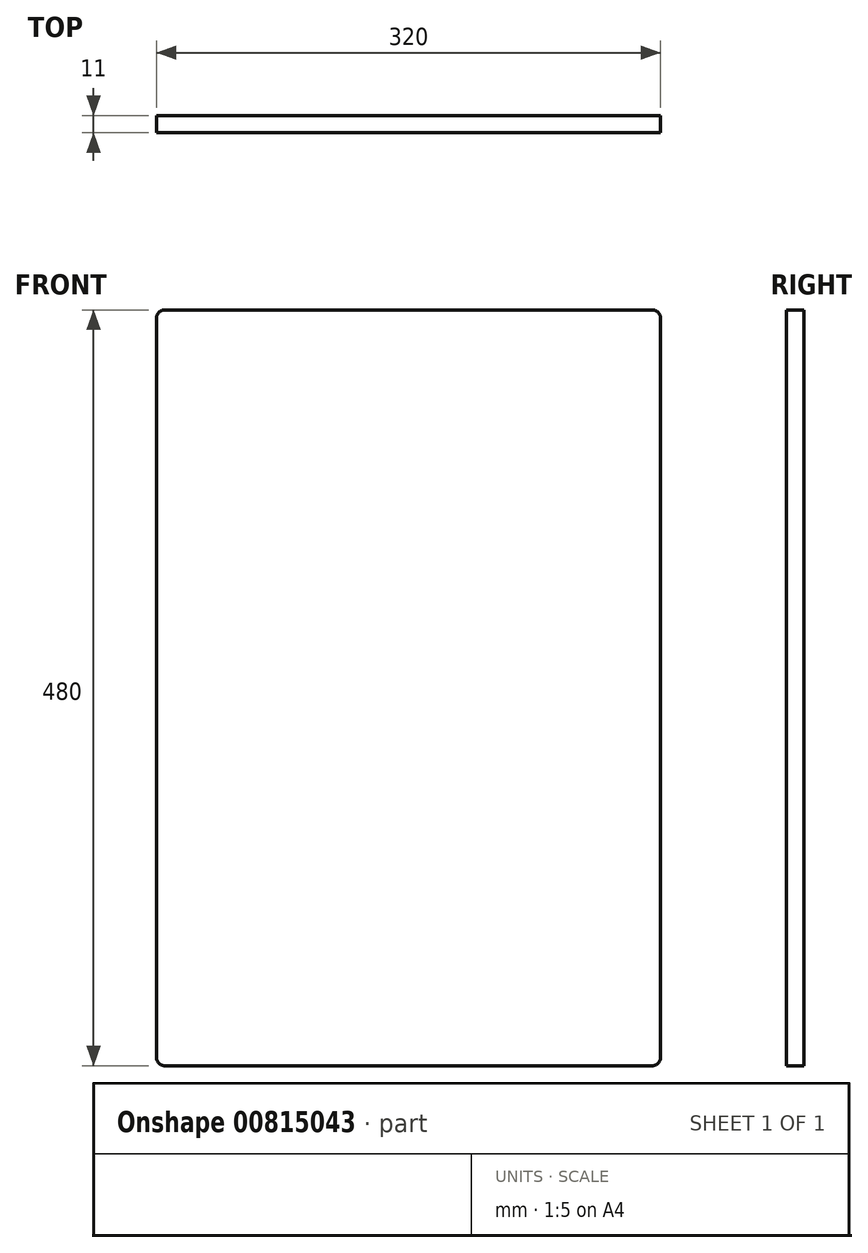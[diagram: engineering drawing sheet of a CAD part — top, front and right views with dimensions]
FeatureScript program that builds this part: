
annotation { "Feature Type Name" : "Feature", "Feature Type Description" : "" }
export const myFeature = defineFeature(function(context is Context, id is Id, definition is map)
    precondition{}
    {
        {
            var Q0;
            Q0=qCreatedBy(makeId("Front.planeOp"),FACE);
            var sketch = newSketch(context, id + "F0", { "sketchPlane" : qUnion([Q0])});
            skLineSegment(sketch, "E0.bottom", {"start": v(5, 0) * mm, "end": v(315, 0) * mm});
            skLineSegment(sketch, "E0.top", {"start": v(5, 480) * mm, "end": v(315, 480) * mm});
            skLineSegment(sketch, "E0.left", {"start": v(0, 5) * mm, "end": v(0, 475) * mm});
            skLineSegment(sketch, "E0.right", {"start": v(320, 5) * mm, "end": v(320, 475) * mm});
            skPoint(sketch, "E1.visualSharp", {"position": v(320, 480) * mm});
            skArc(sketch, "E1.filletArc", {"start": v(320, 475) * mm, "mid": v(318.54, 478.54) * mm, "end": v(315, 480) * mm});
            skPoint(sketch, "E2.visualSharp", {"position": v(0, 480) * mm});
            skArc(sketch, "E2.filletArc", {"start": v(5, 480) * mm, "mid": v(1.46, 478.54) * mm, "end": v(0, 475) * mm});
            skPoint(sketch, "E3.visualSharp", {"position": v(0, 0) * mm});
            skArc(sketch, "E3.filletArc", {"start": v(0, 5) * mm, "mid": v(1.46, 1.46) * mm, "end": v(5, 0) * mm});
            skPoint(sketch, "E4.visualSharp", {"position": v(320, 0) * mm});
            skArc(sketch, "E4.filletArc", {"start": v(315, 0) * mm, "mid": v(318.54, 1.46) * mm, "end": v(320, 5) * mm});
            skSolve(sketch);
        }
        {
            var Q0;
            Q0=makeQuery(id+"F0.imprint","IMPRINT",FACE,{"disambiguationData":[TD([[makeQuery(id+"F0.imprint","IMPRINT",EDGE,{"derivedFrom":sQuery(id+"F0.wireOp",EDGE,"E0.bottom")}),1.0]])]});
            extrude(context, id + "F1", {"entities" : qUnion([Q0]), "depth" : 11 * mm, "offsetDistance" : 25 * mm});
        }
    });
